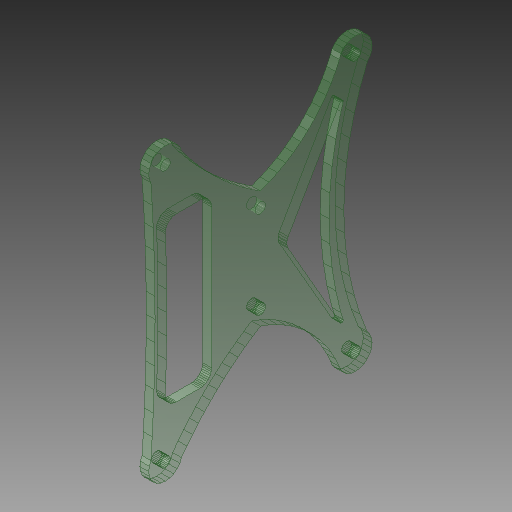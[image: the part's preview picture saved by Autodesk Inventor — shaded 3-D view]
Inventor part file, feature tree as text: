
AUTODESK INVENTOR PART (.ipt)
format: ipt  version: 2018 (Build 220112000, 112)  size: 563,200 bytes
history: native  units: mm
features: extrude x3, sketch x3
ambient origin geometry x8: Origin, YZ Plane, XZ Plane, XY Plane, X Axis, Y Axis, Z Axis, Center Point
bodies: Solid1 (feature_tree)
feature tree (6):
  extrude  "Extrusion1"  Depth=3.0mm
  extrude  "Extrusion2"  Depth=3.0mm
  extrude  "Extrusion3"  [1 undecoded]
  sketch  "Sketch1"  dims[d0=3.0mm d1=0.0mm d2=3.4mm]
  sketch  "Sketch2"  dims[d3=3.0mm d4=0.0mm d5=3.5mm]
  sketch  "Sketch3"  dims[d6=10.0mm d7=0.0mm]
note: 1 required parameter value undecoded (feature->parameter linkage not recoverable at this tier; creation-order binding heuristic only, values carry confidence <= 0.55)
